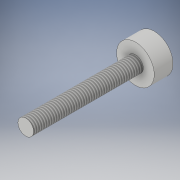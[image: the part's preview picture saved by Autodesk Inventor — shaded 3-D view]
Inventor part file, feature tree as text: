
AUTODESK INVENTOR PART (.ipt)
format: ipt  version: 2018 (Build 220112000, 112)  size: 107,520 bytes
history: native  units: in
note: dims shown in document units (in); Inventor stores cm internally (conversion verified against a paired STEP export)
features: revolve x1, thread x1, sketch x1
ambient origin geometry x8: Origin, YZ Plane, XZ Plane, XY Plane, X Axis, Y Axis, Z Axis, Center Point
bodies: Solid1 (feature_tree)
feature tree (3):
  revolve  "Revolution1"  [1 undecoded]
  thread  "Thread1"  [1 undecoded]
  sketch  "Sketch1"  dims[d0=0.0984in d1=1.378in d2=0.2362in d3=0.2362in d4=90.0deg d5=0.3937in d6=0.0in]
note: 2 required parameter values undecoded (feature->parameter linkage not recoverable at this tier; creation-order binding heuristic only, values carry confidence <= 0.55)